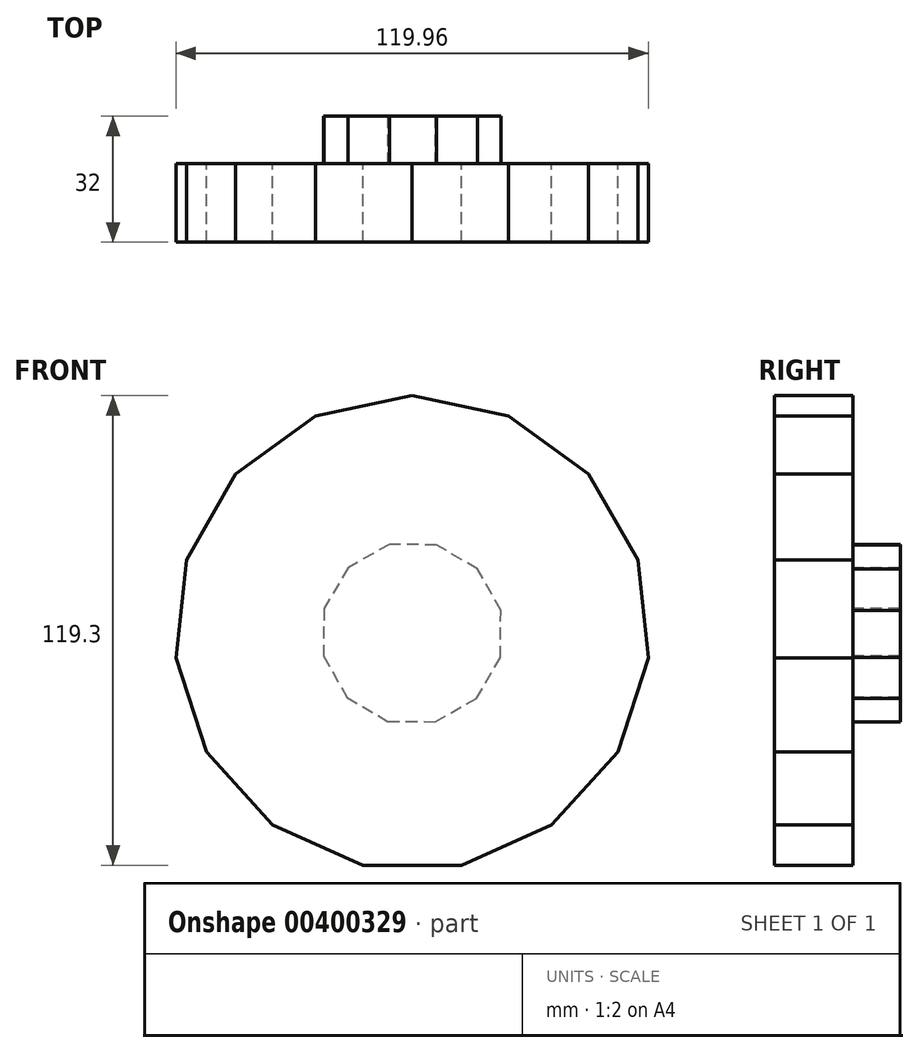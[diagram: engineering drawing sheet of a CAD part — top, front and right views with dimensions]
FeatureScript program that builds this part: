
annotation { "Feature Type Name" : "Feature", "Feature Type Description" : "" }
export const myFeature = defineFeature(function(context is Context, id is Id, definition is map)
    precondition{}
    {
        {
            var Q0;
            Q0=qCreatedBy(makeId("Front.planeOp"),FACE);
            var Q1;
            Q1 = qBodyType(qCreatedBy(id + "FH0l7sb28v6HHdL_0" ,EDGE), BodyType.WIRE);
            cPlane(context, id + "F0", {"entities" : qUnion([Q0, Q1]), "cplaneType" : CPlaneType.OFFSET, "offset" : 25.4 * mm, "width" : 152.4 * mm, "height" : 152.4 * mm});
        }
        {
            var Q0;
            Q0=qCreatedBy(id+"F0.planeOp",FACE);
            var sketch = newSketch(context, id + "F1", { "sketchPlane" : qUnion([Q0])});
            skCircle(sketch, "E0.cCircle", {"center": v(0, 0) * mm, "radius": 59 * mm, "construction": true});
            skLineSegment(sketch, "E0.0", {"start": v(12.54, -59) * mm, "end": v(-12.54, -59) * mm});
            skLineSegment(sketch, "E0.1", {"start": v(-12.54, -59) * mm, "end": v(-35.45, -48.8) * mm});
            skLineSegment(sketch, "E0.2", {"start": v(-35.45, -48.8) * mm, "end": v(-52.23, -30.16) * mm});
            skLineSegment(sketch, "E0.3", {"start": v(-52.23, -30.16) * mm, "end": v(-59.98, -6.3) * mm});
            skLineSegment(sketch, "E0.4", {"start": v(-59.98, -6.3) * mm, "end": v(-57.36, 18.64) * mm});
            skLineSegment(sketch, "E0.5", {"start": v(-57.36, 18.64) * mm, "end": v(-44.82, 40.36) * mm});
            skLineSegment(sketch, "E0.6", {"start": v(-44.82, 40.36) * mm, "end": v(-24.53, 55.1) * mm});
            skLineSegment(sketch, "E0.7", {"start": v(-24.53, 55.1) * mm, "end": v(0, 60.31) * mm});
            skLineSegment(sketch, "E0.8", {"start": v(0, 60.31) * mm, "end": v(24.53, 55.1) * mm});
            skLineSegment(sketch, "E0.9", {"start": v(24.53, 55.1) * mm, "end": v(44.82, 40.36) * mm});
            skLineSegment(sketch, "E0.10", {"start": v(44.82, 40.36) * mm, "end": v(57.36, 18.64) * mm});
            skLineSegment(sketch, "E0.11", {"start": v(57.36, 18.64) * mm, "end": v(59.98, -6.3) * mm});
            skLineSegment(sketch, "E0.12", {"start": v(59.98, -6.3) * mm, "end": v(52.23, -30.16) * mm});
            skLineSegment(sketch, "E0.13", {"start": v(52.23, -30.16) * mm, "end": v(35.45, -48.8) * mm});
            skLineSegment(sketch, "E0.14", {"start": v(35.45, -48.8) * mm, "end": v(12.54, -59) * mm});
            skPoint(sketch, "E0.0.midPoint", {"position": v(0, -59) * mm});
            skSolve(sketch);
        }
        {
            var Q0;
            Q0=makeQuery(id+"F1.imprint","IMPRINT",FACE,{"disambiguationData":[TD([[makeQuery(id+"F1.imprint","IMPRINT",EDGE,{"derivedFrom":sQuery(id+"F1.wireOp",EDGE,"E0.0")}),-1.0]])]});
            var sketch = newSketch(context, id + "F2", { "sketchPlane" : qUnion([Q0])});
            skCircle(sketch, "E1", {"center": v(0, 0) * mm, "radius": 39.9 * mm});
            skSolve(sketch);
        }
        {
            var Q0;
            Q0=makeQuery(id+"F1.imprint","IMPRINT",FACE,{"disambiguationData":[TD([[makeQuery(id+"F1.imprint","IMPRINT",EDGE,{"derivedFrom":sQuery(id+"F1.wireOp",EDGE,"E0.0")}),-1.0]])]});
            var Q1;
            Q1=makeQuery(id+"F2.imprint","IMPRINT",FACE,{"disambiguationData":[TD([[makeQuery(id+"F2.imprint","IMPRINT",EDGE,{"derivedFrom":sQuery(id+"F2.wireOp",EDGE,"E1")}),1.0]])]});
            var Q2;
            Q2=makeQuery(id+"F2.imprint","IMPRINT",FACE,{"disambiguationData":[TD([[makeQuery(id+"F2.imprint","IMPRINT",EDGE,{"derivedFrom":sQuery(id+"F2.wireOp",EDGE,"E1")}),-1.0]])]});
            extrude(context, id + "F3", {"entities" : qUnion([Q0, Q1, Q2]), "depth" : 20 * mm});
        }
        {
            var Q0;
            {var subQ0=sQuery(id+"F1.wireOp",EDGE,"E0.14");var subQ1=sQuery(id+"F1.wireOp",EDGE,"E0.13");var subQ2=sQuery(id+"F1.wireOp",EDGE,"E0.12");var subQ3=sQuery(id+"F1.wireOp",EDGE,"E0.11");var subQ4=sQuery(id+"F1.wireOp",EDGE,"E0.10");var subQ5=sQuery(id+"F1.wireOp",EDGE,"E0.9");var subQ6=sQuery(id+"F1.wireOp",EDGE,"E0.8");var subQ7=sQuery(id+"F1.wireOp",EDGE,"E0.7");var subQ8=sQuery(id+"F1.wireOp",EDGE,"E0.6");var subQ9=sQuery(id+"F1.wireOp",EDGE,"E0.5");var subQ10=sQuery(id+"F1.wireOp",EDGE,"E0.4");var subQ11=sQuery(id+"F1.wireOp",EDGE,"E0.3");var subQ12=sQuery(id+"F1.wireOp",EDGE,"E0.2");var subQ13=sQuery(id+"F1.wireOp",EDGE,"E0.1");var subQ14=sQuery(id+"F1.wireOp",EDGE,"E0.0");Q0=makeQuery(id+"F3.opExtrude","CAP_FACE",FACE,{"disambiguationData":[OSD([subQ14,subQ13,subQ12,subQ11,subQ10,subQ9,subQ8,subQ7,subQ6,subQ5,subQ4,subQ3,subQ2,subQ1,subQ0]),TDD([makeQuery(id+"F1.imprint","IMPRINT",EDGE,{"derivedFrom":subQ14}),makeQuery(id+"F1.imprint","IMPRINT",EDGE,{"derivedFrom":subQ13}),makeQuery(id+"F1.imprint","IMPRINT",EDGE,{"derivedFrom":subQ12}),makeQuery(id+"F1.imprint","IMPRINT",EDGE,{"derivedFrom":subQ11}),makeQuery(id+"F1.imprint","IMPRINT",EDGE,{"derivedFrom":subQ10}),makeQuery(id+"F1.imprint","IMPRINT",EDGE,{"derivedFrom":subQ9}),makeQuery(id+"F1.imprint","IMPRINT",EDGE,{"derivedFrom":subQ8}),makeQuery(id+"F1.imprint","IMPRINT",EDGE,{"derivedFrom":subQ7}),makeQuery(id+"F1.imprint","IMPRINT",EDGE,{"derivedFrom":subQ6}),makeQuery(id+"F1.imprint","IMPRINT",EDGE,{"derivedFrom":subQ5}),makeQuery(id+"F1.imprint","IMPRINT",EDGE,{"derivedFrom":subQ4}),makeQuery(id+"F1.imprint","IMPRINT",EDGE,{"derivedFrom":subQ3}),makeQuery(id+"F1.imprint","IMPRINT",EDGE,{"derivedFrom":subQ2}),makeQuery(id+"F1.imprint","IMPRINT",EDGE,{"derivedFrom":subQ1}),makeQuery(id+"F1.imprint","IMPRINT",EDGE,{"derivedFrom":subQ0})])],"isStart":true});}
            var sketch = newSketch(context, id + "F4", { "sketchPlane" : qUnion([Q0])});
            skCircle(sketch, "E2.cCircle", {"center": v(0, 0) * mm, "radius": 22.47 * mm, "construction": true});
            skLineSegment(sketch, "E2.0", {"start": v(-16.6, 16.3) * mm, "end": v(-6.23, 22.4) * mm});
            skLineSegment(sketch, "E2.1", {"start": v(-6.23, 22.4) * mm, "end": v(5.8, 22.52) * mm});
            skLineSegment(sketch, "E2.2", {"start": v(5.8, 22.52) * mm, "end": v(16.3, 16.6) * mm});
            skLineSegment(sketch, "E2.3", {"start": v(16.3, 16.6) * mm, "end": v(22.4, 6.23) * mm});
            skLineSegment(sketch, "E2.4", {"start": v(22.4, 6.23) * mm, "end": v(22.52, -5.8) * mm});
            skLineSegment(sketch, "E2.5", {"start": v(22.52, -5.8) * mm, "end": v(16.6, -16.3) * mm});
            skLineSegment(sketch, "E2.6", {"start": v(16.6, -16.3) * mm, "end": v(6.23, -22.4) * mm});
            skLineSegment(sketch, "E2.7", {"start": v(6.23, -22.4) * mm, "end": v(-5.8, -22.52) * mm});
            skLineSegment(sketch, "E2.8", {"start": v(-5.8, -22.52) * mm, "end": v(-16.3, -16.6) * mm});
            skLineSegment(sketch, "E2.9", {"start": v(-16.3, -16.6) * mm, "end": v(-22.4, -6.23) * mm});
            skLineSegment(sketch, "E2.10", {"start": v(-22.4, -6.23) * mm, "end": v(-22.52, 5.8) * mm});
            skLineSegment(sketch, "E2.11", {"start": v(-22.52, 5.8) * mm, "end": v(-16.6, 16.3) * mm});
            skPoint(sketch, "E2.0.midPoint", {"position": v(-11.42, 19.35) * mm});
            skSolve(sketch);
        }
        {
            var Q0;
            Q0=makeQuery(id+"F4.imprint","IMPRINT",FACE,{"disambiguationData":[TD([[makeQuery(id+"F4.imprint","IMPRINT",EDGE,{"derivedFrom":sQuery(id+"F4.wireOp",EDGE,"E2.0")}),-1.0]])]});
            extrude(context, id + "F5", {"entities" : qUnion([Q0]), "depth" : 12 * mm});
        }
    });
